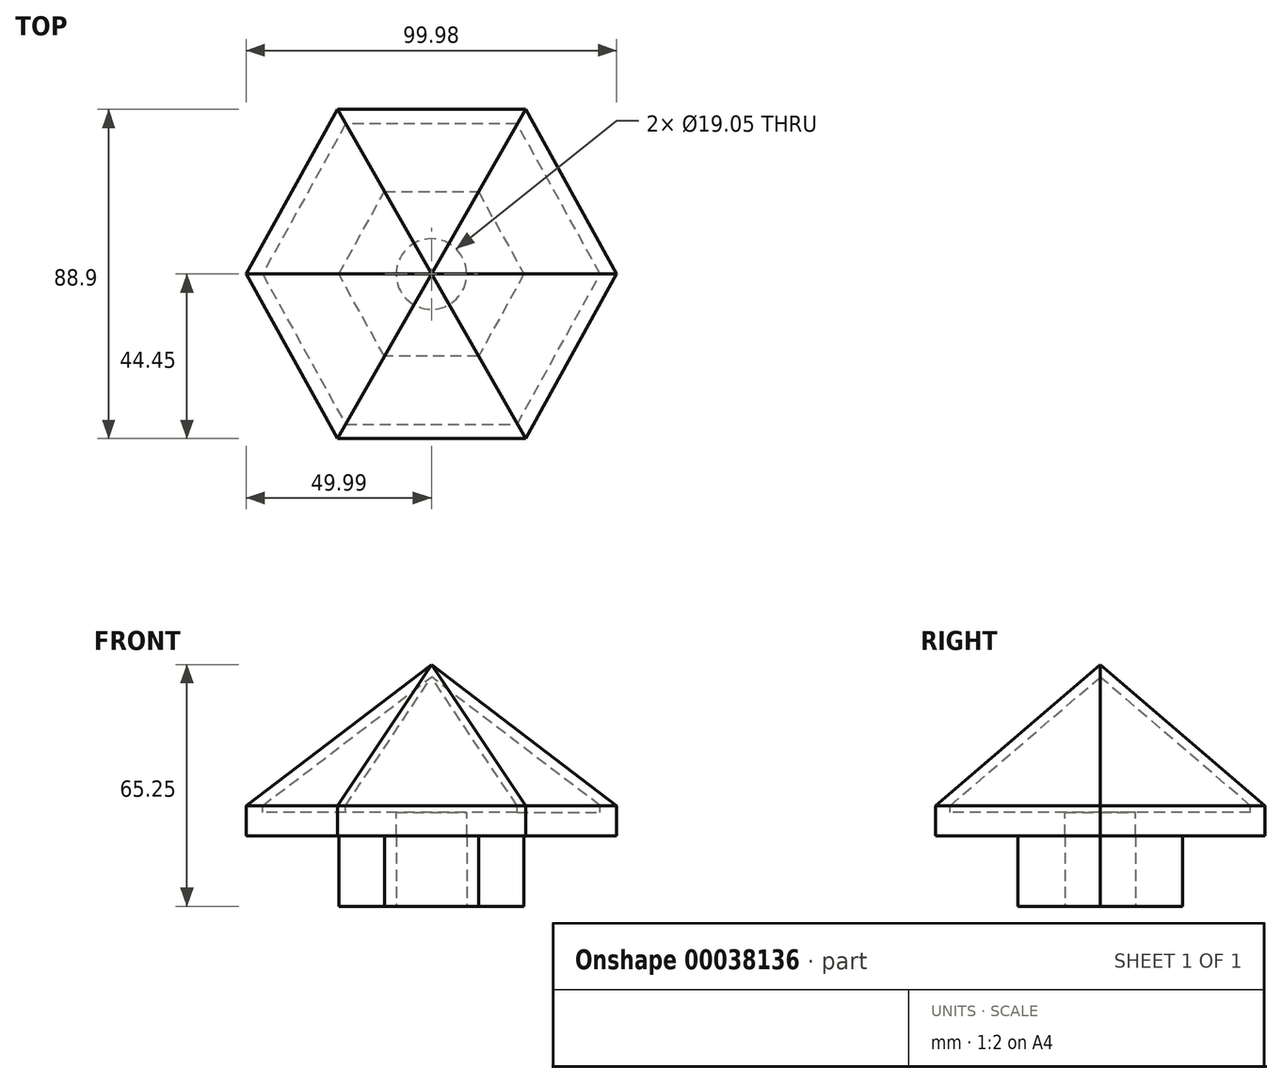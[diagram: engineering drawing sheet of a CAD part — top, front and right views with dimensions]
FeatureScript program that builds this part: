
annotation { "Feature Type Name" : "Feature", "Feature Type Description" : "" }
export const myFeature = defineFeature(function(context is Context, id is Id, definition is map)
    precondition{}
    {
        {
            var Q0;
            Q0=qCreatedBy(makeId("Top.planeOp"),FACE);
            var sketch = newSketch(context, id + "F0", { "sketchPlane" : qUnion([Q0])});
            skLineSegment(sketch, "E0", {"start": v(-25.4, 44.45) * mm, "end": v(25.4, 44.45) * mm});
            skLineSegment(sketch, "E1", {"start": v(25.4, 44.45) * mm, "end": v(50, 0) * mm});
            skLineSegment(sketch, "E2", {"start": v(50, 0) * mm, "end": v(25.4, -44.45) * mm});
            skLineSegment(sketch, "E3", {"start": v(25.4, -44.45) * mm, "end": v(-25.4, -44.45) * mm});
            skLineSegment(sketch, "E4", {"start": v(-25.4, -44.45) * mm, "end": v(-50, 0) * mm});
            skLineSegment(sketch, "E5", {"start": v(-50, 0) * mm, "end": v(-25.4, 44.45) * mm});
            skLineSegment(sketch, "E6", {"start": v(0, 84.7) * mm, "end": v(0, -73.8) * mm, "construction": true});
            skSolve(sketch);
        }
        {
            assignVariable(context, id + "F1", {"name" : "Flat", "anyValue" : 1.75});
        }
        {
            var Q0;
            Q0=qCreatedBy(makeId("Top.planeOp"),FACE);
            cPlane(context, id + "F2", {"entities" : qUnion([Q0]), "cplaneType" : CPlaneType.OFFSET, "offset" : 38.1 * mm, "width" : 152.4 * mm, "height" : 152.4 * mm});
        }
        {
            var Q0;
            Q0=qCreatedBy(id+"F2.planeOp",FACE);
            var sketch = newSketch(context, id + "F3", { "sketchPlane" : qUnion([Q0])});
            skPoint(sketch, "E7", {"position": v(0, 0) * mm});
            skSolve(sketch);
        }
        {
            var Q0;
            Q0 = qSketchRegion(id + "F0", true);
            var Q1;
            Q1=sQuery(id+"F3.wireOp",VERTEX,"E7");
            loft(context, id + "F4", {"sheetProfilesArray" : [{ "sheetProfileEntities" : qUnion([Q0]) }, { "sheetProfileEntities" : qUnion([Q1]) }]});
        }
        {
            var Q0;
            Q0=makeQuery(id+"F4.opLoft","CAP_FACE",FACE,{"disambiguationData":[OSD([makeQuery(id+"F0.imprint","IMPRINT",FACE,{"disambiguationData":[TD([[makeQuery(id+"F0.imprint","IMPRINT",EDGE,{"derivedFrom":sQuery(id+"F0.wireOp",EDGE,"E0")}),-1.0]])]})])],"isStart":true});
            shell(context, id + "F5", {"entities" : qUnion([Q0]), "thickness" : 2.54 * mm});
        }
        {
            var Q0;
            Q0=qCreatedBy(makeId("Top.planeOp"),FACE);
            var sketch = newSketch(context, id + "F6", { "sketchPlane" : qUnion([Q0])});
            skLineSegment(sketch, "E8.0", {"start": v(-23.14, 40.55) * mm, "end": v(-45.57, 0) * mm});
            skLineSegment(sketch, "E9.0", {"start": v(-25.4, 44.45) * mm, "end": v(-50, 0) * mm});
            skLineSegment(sketch, "E10.0", {"start": v(25.4, 44.45) * mm, "end": v(-25.4, 44.45) * mm});
            skLineSegment(sketch, "E11.0", {"start": v(23.14, 40.55) * mm, "end": v(-23.14, 40.55) * mm});
            skLineSegment(sketch, "E12.0", {"start": v(45.57, 0) * mm, "end": v(23.14, 40.55) * mm});
            skLineSegment(sketch, "E13.0", {"start": v(50, 0) * mm, "end": v(25.4, 44.45) * mm});
            skLineSegment(sketch, "E14.0", {"start": v(25.4, -44.45) * mm, "end": v(50, 0) * mm});
            skLineSegment(sketch, "E15.0", {"start": v(23.14, -40.55) * mm, "end": v(45.57, 0) * mm});
            skLineSegment(sketch, "E16.0", {"start": v(-25.4, -44.45) * mm, "end": v(25.4, -44.45) * mm});
            skLineSegment(sketch, "E17.0", {"start": v(-23.14, -40.55) * mm, "end": v(23.14, -40.55) * mm});
            skLineSegment(sketch, "E18.0", {"start": v(-45.57, 0) * mm, "end": v(-23.14, -40.55) * mm});
            skLineSegment(sketch, "E19.0", {"start": v(-50, 0) * mm, "end": v(-25.4, -44.45) * mm});
            skSolve(sketch);
        }
        {
            var Q0;
            Q0 = qSketchRegion(id + "F6", true);
            extrude(context, id + "F7", {"entities" : qUnion([Q0]), "operationType" : NewBodyOperationType.ADD, "oppositeDirection" : true, "depth" : (getVariable(context, 'Flat')) * mm});
        }
        {
            var Q0;
            Q0=makeQuery(id+"F7.opExtrude","CAP_FACE",FACE,{"disambiguationData":[OSD([sQuery(id+"F6.wireOp",EDGE,"E8.0"),sQuery(id+"F6.wireOp",EDGE,"E9.0"),sQuery(id+"F6.wireOp",EDGE,"E10.0"),sQuery(id+"F6.wireOp",EDGE,"E11.0"),sQuery(id+"F6.wireOp",EDGE,"E12.0"),sQuery(id+"F6.wireOp",EDGE,"E13.0"),sQuery(id+"F6.wireOp",EDGE,"E14.0"),sQuery(id+"F6.wireOp",EDGE,"E15.0"),sQuery(id+"F6.wireOp",EDGE,"E16.0"),sQuery(id+"F6.wireOp",EDGE,"E17.0"),sQuery(id+"F6.wireOp",EDGE,"E18.0"),sQuery(id+"F6.wireOp",EDGE,"E19.0")])],"isStart":false});
            var sketch = newSketch(context, id + "F8", { "sketchPlane" : qUnion([Q0])});
            skLineSegment(sketch, "E20.0", {"start": v(25.4, 44.45) * mm, "end": v(50, 0) * mm});
            skLineSegment(sketch, "E21.0", {"start": v(50, 0) * mm, "end": v(25.4, -44.45) * mm});
            skLineSegment(sketch, "E22.0", {"start": v(25.4, -44.45) * mm, "end": v(-25.4, -44.45) * mm});
            skLineSegment(sketch, "E23.0", {"start": v(-25.4, -44.45) * mm, "end": v(-50, 0) * mm});
            skLineSegment(sketch, "E24.0", {"start": v(-50, 0) * mm, "end": v(-25.4, 44.45) * mm});
            skLineSegment(sketch, "E25.0", {"start": v(-25.4, 44.45) * mm, "end": v(25.4, 44.45) * mm});
            skCircle(sketch, "E26", {"center": v(0, 0) * mm, "radius": 9.53 * mm});
            skSolve(sketch);
        }
        {
            var Q0;
            Q0=makeQuery(id+"F8.imprint","IMPRINT",FACE,{"disambiguationData":[TD([[makeQuery(id+"F8.imprint","IMPRINT",EDGE,{"derivedFrom":sQuery(id+"F8.wireOp",EDGE,"344dd562-a590-4f2f-9bf3-a6f47775fa42.0")}),1.0]])]});
            var Q1;
            Q1=makeQuery(id+"F8.imprint","IMPRINT",FACE,{"disambiguationData":[TD([[makeQuery(id+"F8.imprint","IMPRINT",EDGE,{"derivedFrom":sQuery(id+"F8.wireOp",EDGE,"E20.0")}),-1.0]])]});
            cPlane(context, id + "F9", {"entities" : qUnion([Q0, Q1]), "cplaneType" : CPlaneType.OFFSET, "offset" : 25.4 * mm, "width" : 152.4 * mm, "height" : 152.4 * mm});
        }
        {
            var Q0;
            Q0=qCreatedBy(id+"F9.planeOp",FACE);
            var sketch = newSketch(context, id + "F10", { "sketchPlane" : qUnion([Q0])});
            skLineSegment(sketch, "E27", {"start": v(-25, 0) * mm, "end": v(-12.7, 22.23) * mm});
            skLineSegment(sketch, "E28", {"start": v(-12.7, 22.23) * mm, "end": v(12.7, 22.22) * mm});
            skLineSegment(sketch, "E29", {"start": v(12.7, 22.22) * mm, "end": v(25, 0) * mm});
            skLineSegment(sketch, "E30", {"start": v(25, 0) * mm, "end": v(12.7, -22.23) * mm});
            skLineSegment(sketch, "E31", {"start": v(12.7, -22.23) * mm, "end": v(-12.7, -22.22) * mm});
            skLineSegment(sketch, "E32", {"start": v(-12.7, -22.23) * mm, "end": v(-25, 0) * mm});
            skCircle(sketch, "E33", {"center": v(0, 0) * mm, "radius": 9.53 * mm});
            skSolve(sketch);
        }
        {
            var Q0;
            Q0 = qSketchRegion(id + "F8", true);
            extrude(context, id + "F11", {"entities" : qUnion([Q0]), "operationType" : NewBodyOperationType.ADD, "depth" : 6.35 * mm});
        }
        {
            var Q0;
            Q0=makeQuery(id+"F10.imprint","IMPRINT",FACE,{"disambiguationData":[TD([[makeQuery(id+"F10.imprint","IMPRINT",EDGE,{"derivedFrom":sQuery(id+"F10.wireOp",EDGE,"E27")}),-1.0]])]});
            extrude(context, id + "F12", {"entities" : qUnion([Q0]), "endBound" : BoundingType.UP_TO_NEXT, "oppositeDirection" : true, "depth" : 25.4 * mm});
        }
    });
